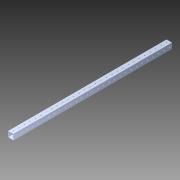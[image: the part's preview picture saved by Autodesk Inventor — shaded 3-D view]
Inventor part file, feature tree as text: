
AUTODESK INVENTOR PART (.ipt)
format: ipt  version: 2014 (Build 180170000, 170)  size: 1,345,024 bytes
history: native  units: in
note: dims shown in document units (in); Inventor stores cm internally (conversion verified against a paired STEP export)
features: extrude x2, sketch x2, pattern_circular x1, other x1, fillet x1, imported_body x1
ambient origin geometry x8: Origin, YZ Plane, XZ Plane, XY Plane, X Axis, Y Axis, Z Axis, Center Point
bodies: Body1 (feature_tree)
feature tree (8):
  pattern_circular  "CirPattern2"
  other  "1x1 tube1"
  extrude  "Extrusion1"  Depth=0.0787in
  fillet  "Fillet1"  Radius=1.0in
  extrude  "Extrusion3"  [1 undecoded]
  imported_body  "Base1"
  sketch  "Sketch1"  dims[d0=30.0in d1=0.0in d4=0.0787in d5=1.0in d6=0.0in]
  sketch  "Sketch4"
note: 1 required parameter value undecoded (feature->parameter linkage not recoverable at this tier; creation-order binding heuristic only, values carry confidence <= 0.55)
